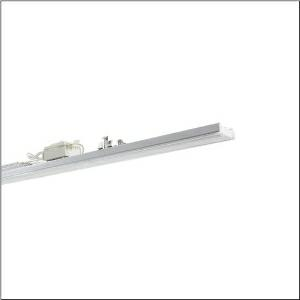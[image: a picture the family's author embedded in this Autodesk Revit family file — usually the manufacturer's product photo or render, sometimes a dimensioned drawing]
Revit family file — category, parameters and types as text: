
# Revit family: licross_11_recessed_mo_51tl12dn455g
name_source: partatom
category: Lighting Fixtures
units: mm (PartAtom-declared; Revit-internal decimal feet)

## family parameters
Cut with Voids When Loaded = No
Host = Face
Light Source = No
Part Type = Normal
Room Calculation Point = No
Round Connector Dimension = Use Diameter
Shared = No

## types (1)
- --- (1 x LED, 5700 lm, 29.9 W, 4000K)
    Apparent Load = 30 VA
    CIE Flux Codes = 67 92 99 100 100
    Color Rendering = 80
    Color Temperature = 4000K
    Default Elevation = 1800 mm
    Description = Licross 11 Recessed MO, luminaire insert, of sheet steel, coil coated, white, length: 1.500mm, width: 66mm, height: 67mm, LED rated luminous flux: 5.700lm, light colour: 840, SDCM (Standard Deviation of Colour Matching)MacAdam ≤ 2 SDCM (initial), control gear: DALI 2, with plug, 5-pole, with phase selection, mains connection: 220..240V, AC, 50/60Hz, rated input power: 30W, internal wiring halogen-free, primary optical cover: cover, of PMMA, light emission: direct distribution, primary light characteristic: symmetric, protection rating (complete): IP40, insulation class (complete): insulation class I (protective earthing), certification: CE, ENEC, VDE, UKCA, protection symbol: D if used in an environment without relevant dust loads with corresponding accessories, impact resistance: IK06, permissible ambient temperature for indoor applications: -25..+45°C, corresponds to IFS (International Featured Standards) requirements for safety and quality in the food industry, reducing of maximum allowable ambient temperature of 5°C with ceiling mounting, LABS conformity tested according to VDMA 24364:2018-05, The light source and the operating device comply with the requirements of the Ecodesign Regulation (EU) 2019/2020 and are replaceable in accordance with this regulation, packaging unit: 1 piece
    Height = 58 mm
    Lamp = 1 x LED
    Lamp Light Flux = 5700 lm
    Lamp Power = 29.9 W
    Lamp count = 1
    Length = 1500 mm
    Luminous efficacy = 191 lm/W
    Manufacturer = Siteco
    ModVariant = No
    Model = 51TL12DN455G
    Mounting Place = Ceiling
    Mounting Type = Pendant
    Number of Poles = 1
    OnlyDefault = Yes
    Power Factor = 1
    Product Name = Licross 11 Recessed MO
    Product group = luminaire insert | ceiling pendant
    ProductGroupID = 901
    Protection Class = Protection class I
    Protection Degree = IP 40
    RLX_Detail_Level = 1
    RLX_Emergency_Light_Flux = 0 lm
    RLX_Emergency_Type = 0
    RLX_Emergency_Type_DB = No
    RlxData = <blob elided: 24285 chars, md5=451f98be>
    Socket = socket
    Standby Power = 0 W
    System Light Flux = 5700 lm
    System Power = 30 W
    Type Comments = factory setting: luminous flux: 100 % | dim-lin: 254 | 202 mA
    Type Image = l_1296930.jpg
    URL = http://relux.com
    VarID = @adj_101853
    Voltage = 0 V
    Weight = 0.00 kg
    Width = 66 mm

## geometry (parser evidence)
native form markers: Blend x4, Sweep x11
no freeform markers — native parametric forms only
